# Revit family: ShowerCornerSpongeBasket-Double-Vitra-BaseSeries-A44160
name_source: partatom
category: Plumbing Fixtures
revit_build: Autodesk Revit 2017 (Build: 20160225_1515(x64)
units: mm (PartAtom-declared; Revit-internal decimal feet)

## family parameters
Cut with Voids When Loaded = No
Host = Face
OmniClass Number = 23.45.00.00
OmniClass Title = Sanitary, Laundry, and Cleaning Equipment
Part Type = Normal
Room Calculation Point = No
Round Connector Dimension = Use Diameter
Shared = Yes

## types (2) — shared parameters
BIMobject category = Sanitary - Bathroom Accessories
Brand = VitrA
CW Connection = No
Description = Base Corner Unit - Sponge Basket
Design country = Turkey
HW Connection = No
IFC Classification = Sanitary Terminal
Main Material = Metal
Manufacturer = Vitra
Manufacturer name = Vitra
Masterformat 2014 Code = 01 52 19
Masterformat 2014 Description = Sanitary Facilities
Mounting type = Wall Mounted
NBS Referans Code = 31-75
NBS Referans Description = Sanitary Accessories
Nominal Depth (mm) = 195 mm
Nominal Height (mm) = 340 mm  [stored 1.11549 ft]
Nominal Width (mm) = 192 mm  [stored 0.629921 ft]
OmniClass Code = 23-19 31 17
OmniClass Description = Sanitary Room Units
Product Type = Built-in Shower Corner Basket
Product certification = https://www.vitraglobal.com
Product family = BaseSeries
Product group = Shower Corner Basket
Product url = https://vitraglobal.com
Technical description = https://vitraglobal.com
UNSPSC Code = 301815
URL = https://vitraglobal.com
Uniclass 1.4 Code = L721
Uniclass 1.4 Description = Sanitary equipment
Uniclass 2.0 Code = PR-31-75
Uniclass 2.0 Description = Sanitary Accessories
Uniclass 2015 Code = Pr_40_20
Uniclass 2015 Name = Sanitary fittings and accessories
Uniformat II Code = E1090
Uniformat II Description = Other Equipment
Vent Connection = No
Warranty Period (Year) = 5 years
Waste Connection = No
Weight Net (kg) = 2
Youtube = https://www.youtube.com
zero-valued in all types: Default Elevation

## per-type parameters (varying)
| type | Article No. (default) | Coating Material | Color | Model | Product SKU |
| ShowerCornerSpongeBasket-Double-Vitra-BaseSeries-A44160 | A44160 | Chrome | Chrome | A44160 | A44160 |
| ShowerCornerSpongeBasket-Double-Vitra-BaseSeries-A4416036 | A4416036 | Matte Black (Metal) | Matte Black | A4416036 | A4416036 |

note: [stored X ft] marks values corroborated as IEEE doubles in the binary element streams (Revit-internal decimal feet)

## geometry (parser evidence)
native form markers: Sweep x1
no freeform markers — native parametric forms only
